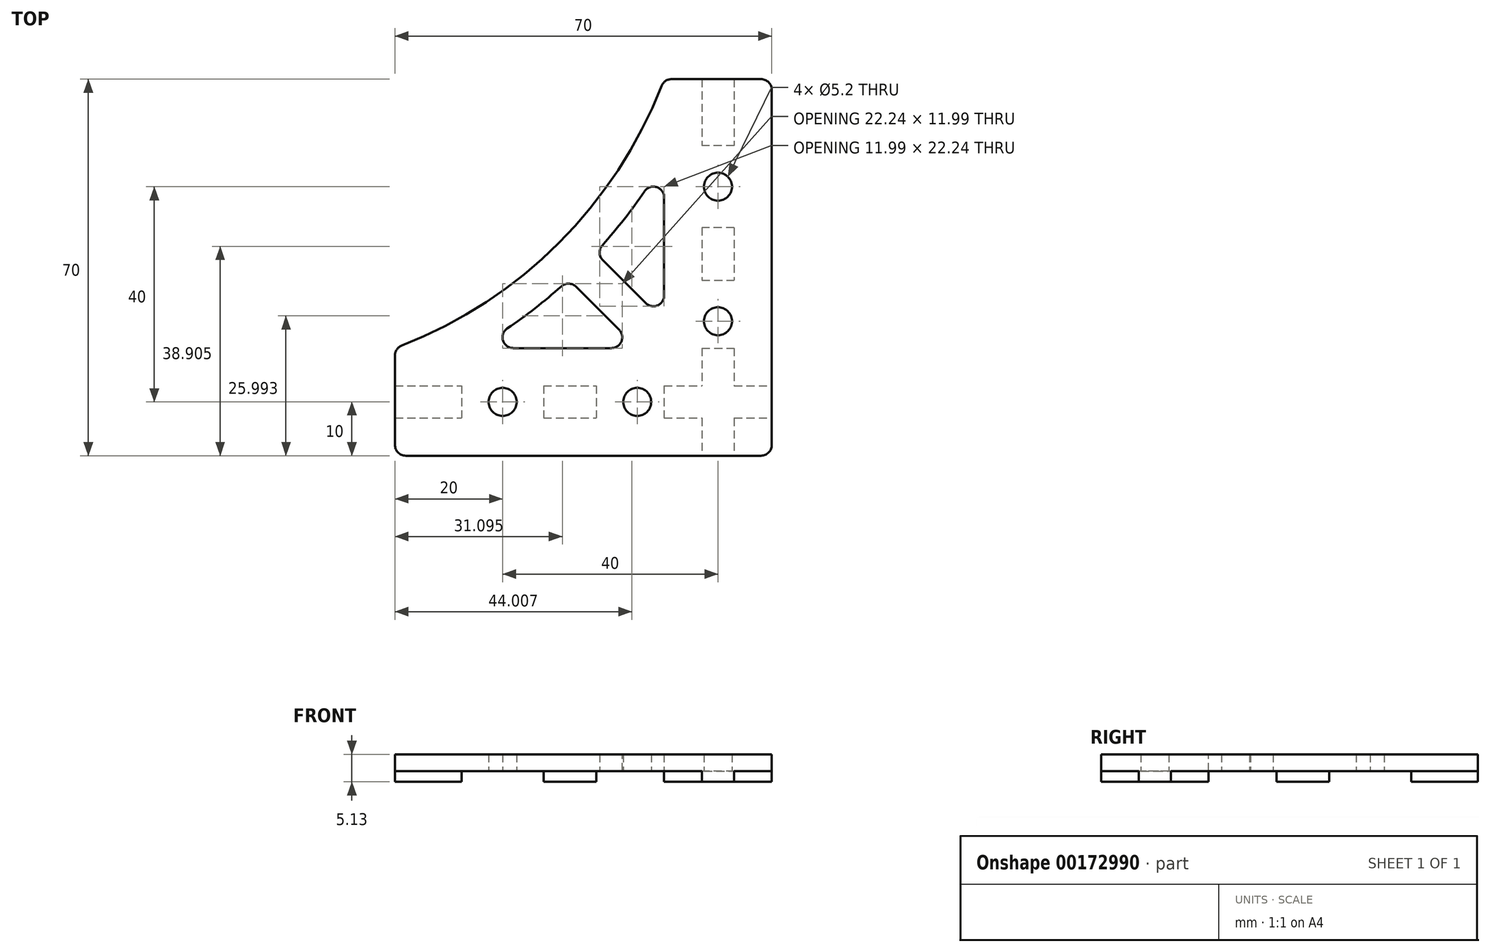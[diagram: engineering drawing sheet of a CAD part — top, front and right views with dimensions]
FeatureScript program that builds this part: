
annotation { "Feature Type Name" : "Feature", "Feature Type Description" : "" }
export const myFeature = defineFeature(function(context is Context, id is Id, definition is map)
    precondition{}
    {
        {
            var Q0;
            Q0=qCreatedBy(makeId("Top.planeOp"),FACE);
            var sketch = newSketch(context, id + "F0", { "sketchPlane" : qUnion([Q0])});
            skLineSegment(sketch, "E0.bottom", {"start": v(-35, 35) * mm, "end": v(35, 35) * mm});
            skLineSegment(sketch, "E0.top", {"start": v(-35, -35) * mm, "end": v(35, -35) * mm});
            skLineSegment(sketch, "E0.left", {"start": v(-35, 35) * mm, "end": v(-35, -35) * mm});
            skLineSegment(sketch, "E0.right", {"start": v(35, 35) * mm, "end": v(35, -35) * mm});
            skPoint(sketch, "E0.middle", {"position": v(0, 0) * mm});
            skLineSegment(sketch, "E1", {"start": v(15, 35) * mm, "end": v(-35, -15) * mm});
            skArc(sketch, "E2", {"start": v(-35, -15) * mm, "mid": v(-4.55, 4.55) * mm, "end": v(15, 35) * mm});
            skSolve(sketch);
        }
        {
            var Q0;
            {var subQ2=sQuery(id+"F0.wireOp",EDGE,"E0.top");Q0=makeQuery(id+"F0.imprint","IMPRINT",FACE,{"disambiguationData":[TD([[makeQuery(id+"F0.imprint","IMPRINT",EDGE,{"derivedFrom":subQ2}),1.0]])]});}
            var Q1;
            {var subQ0=sQuery(id+"F0.wireOp",EDGE,"E0.right");var subQ1=sQuery(id+"F0.wireOp",EDGE,"E0.bottom");var subQ2=makeQuery(id+"F0.imprint","INTERSECT",VERTEX,{"derivedFrom":[subQ1,subQ0]});Q1=makeQuery(id+"F0.imprint","IMPRINT",FACE,{"disambiguationData":[TD([[makeQuery(id+"F0.imprint","IMPRINT",EDGE,{"disambiguationData":[TD([[subQ2,-1.0]])],"derivedFrom":subQ0}),-1.0]])]});}
            var Q2;
            {var subQ1=sQuery(id+"F0.wireOp",EDGE,"E0.right");var subQ5=sQuery(id+"F0.wireOp",EDGE,"E0.top");var subQ6=makeQuery(id+"F0.imprint","INTERSECT",VERTEX,{"derivedFrom":[subQ5,subQ1]});Q2=makeQuery(id+"F0.imprint","IMPRINT",FACE,{"disambiguationData":[TD([[makeQuery(id+"F0.imprint","IMPRINT",EDGE,{"disambiguationData":[TD([[subQ6,1.0]])],"derivedFrom":subQ5}),1.0]])]});}
            extrude(context, id + "F1", {"entities" : qUnion([Q0, Q1, Q2]), "depth" : 3.12 * mm});
        }
        {
            var Q0;
            Q0=makeQuery(id+"F1.opExtrude","CAP_FACE",FACE,{"disambiguationData":[OSD([sQuery(id+"F0.wireOp",EDGE,"E0.bottom"),sQuery(id+"F0.wireOp",EDGE,"E0.top"),sQuery(id+"F0.wireOp",EDGE,"E0.left"),sQuery(id+"F0.wireOp",EDGE,"E0.right"),sQuery(id+"F0.wireOp",EDGE,"E1")])],"isStart":true});
            var sketch = newSketch(context, id + "F2", { "sketchPlane" : qUnion([Q0])});
            skLineSegment(sketch, "E3", {"start": v(25, -35) * mm, "end": v(25, 35) * mm, "construction": true});
            skLineSegment(sketch, "E4", {"start": v(-35, 25) * mm, "end": v(35, 25) * mm, "construction": true});
            skLineSegment(sketch, "E5.bottom", {"start": v(22, -35) * mm, "end": v(28, -35) * mm});
            skLineSegment(sketch, "E5.top", {"start": v(22, 35) * mm, "end": v(28, 35) * mm});
            skLineSegment(sketch, "E5.left", {"start": v(22, -35) * mm, "end": v(22, 35) * mm});
            skLineSegment(sketch, "E5.right", {"start": v(28, -35) * mm, "end": v(28, 35) * mm});
            skPoint(sketch, "E5.middle", {"position": v(25, 0) * mm});
            skLineSegment(sketch, "E6.bottom", {"start": v(-35, 22) * mm, "end": v(35, 22) * mm});
            skLineSegment(sketch, "E6.top", {"start": v(-35, 28) * mm, "end": v(35, 28) * mm});
            skLineSegment(sketch, "E6.left", {"start": v(-35, 22) * mm, "end": v(-35, 28) * mm});
            skLineSegment(sketch, "E6.right", {"start": v(35, 22) * mm, "end": v(35, 28) * mm});
            skPoint(sketch, "E6.middle", {"position": v(0, 25) * mm});
            skLineSegment(sketch, "E7.bottom", {"start": v(22, 22) * mm, "end": v(15, 22) * mm});
            skLineSegment(sketch, "E7.top", {"start": v(22, 28) * mm, "end": v(15, 28) * mm});
            skLineSegment(sketch, "E7.left", {"start": v(22, 22) * mm, "end": v(22, 28) * mm});
            skLineSegment(sketch, "E7.right", {"start": v(15, 22) * mm, "end": v(15, 28) * mm});
            skLineSegment(sketch, "E8.bottom", {"start": v(28, 22) * mm, "end": v(22, 22) * mm});
            skLineSegment(sketch, "E8.top", {"start": v(28, 15) * mm, "end": v(22, 15) * mm});
            skLineSegment(sketch, "E8.left", {"start": v(28, 22) * mm, "end": v(28, 15) * mm});
            skLineSegment(sketch, "E8.right", {"start": v(22, 22) * mm, "end": v(22, 15) * mm});
            skSolve(sketch);
        }
        {
            var Q0;
            {var subQ0=sQuery(id+"F2.wireOp",EDGE,"E5.bottom");Q0=makeQuery(id+"F2.imprint","IMPRINT",FACE,{"disambiguationData":[TD([[makeQuery(id+"F2.imprint","IMPRINT",EDGE,{"derivedFrom":subQ0}),1.0]])]});}
            var Q1;
            {var subQ0=sQuery(id+"F2.wireOp",EDGE,"E6.left");Q1=makeQuery(id+"F2.imprint","IMPRINT",FACE,{"disambiguationData":[TD([[makeQuery(id+"F2.imprint","IMPRINT",EDGE,{"derivedFrom":subQ0}),-1.0]])]});}
            var Q2;
            {var subQ0=sQuery(id+"F2.wireOp",EDGE,"E8.top");Q2=makeQuery(id+"F2.imprint","IMPRINT",FACE,{"disambiguationData":[TD([[makeQuery(id+"F2.imprint","IMPRINT",EDGE,{"derivedFrom":subQ0}),1.0]])]});}
            var Q3;
            {var subQ0=sQuery(id+"F2.wireOp",EDGE,"d9nGMlHh-qkIi-XzYH-rveG-kUuO3HYsBL67");var subQ1=sQuery(id+"F2.wireOp",EDGE,"E5.left");var subQ2=makeQuery(id+"F2.imprint","INTERSECT",VERTEX,{"derivedFrom":[subQ1,subQ0]});Q3=makeQuery(id+"F2.imprint","IMPRINT",FACE,{"disambiguationData":[TD([[makeQuery(id+"F2.imprint","IMPRINT",EDGE,{"disambiguationData":[TD([[subQ2,-1.0]])],"derivedFrom":subQ1}),-1.0]])]});}
            var Q4;
            {var subQ0=sQuery(id+"F2.wireOp",EDGE,"E7.right");Q4=makeQuery(id+"F2.imprint","IMPRINT",FACE,{"disambiguationData":[TD([[makeQuery(id+"F2.imprint","IMPRINT",EDGE,{"derivedFrom":subQ0}),1.0]])]});}
            var Q5;
            {var subQ0=sQuery(id+"F2.wireOp",EDGE,"Tg9qOg1b-ZZ8D-OlWz-hFwT-lKIjL2JHWv4c");var subQ1=sQuery(id+"F2.wireOp",EDGE,"E6.bottom");var subQ2=makeQuery(id+"F2.imprint","INTERSECT",VERTEX,{"derivedFrom":[subQ1,subQ0]});Q5=makeQuery(id+"F2.imprint","IMPRINT",FACE,{"disambiguationData":[TD([[makeQuery(id+"F2.imprint","IMPRINT",EDGE,{"disambiguationData":[TD([[subQ2,-1.0]])],"derivedFrom":subQ1}),1.0]])]});}
            extrude(context, id + "F3", {"entities" : qUnion([Q0, Q1, Q2, Q3, Q4, Q5]), "operationType" : NewBodyOperationType.ADD, "depth" : 2 * mm, "offsetDistance" : 25 * mm});
        }
        {
            var Q0;
            Q0=makeQuery(id+"F3.opExtrude","CAP_FACE",FACE,{"disambiguationData":[OSD([sQuery(id+"F2.wireOp",EDGE,"E5.bottom"),sQuery(id+"F2.wireOp",EDGE,"E5.left"),sQuery(id+"F2.wireOp",EDGE,"E5.right"),sQuery(id+"F2.wireOp",EDGE,"E8.top")])],"isStart":false});
            var sketch = newSketch(context, id + "F4", { "sketchPlane" : qUnion([Q0])});
            skCircle(sketch, "E9", {"center": v(25, -15) * mm, "radius": 2.6 * mm});
            skCircle(sketch, "E10", {"center": v(25, 10) * mm, "radius": 2.6 * mm});
            skCircle(sketch, "E11", {"center": v(10, 25) * mm, "radius": 2.6 * mm});
            skCircle(sketch, "E12", {"center": v(-15, 25) * mm, "radius": 2.6 * mm});
            skSolve(sketch);
        }
        {
            var Q0;
            Q0=makeQuery(id+"F4.imprint","IMPRINT",FACE,{"disambiguationData":[TD([[makeQuery(id+"F4.imprint","IMPRINT",EDGE,{"derivedFrom":sQuery(id+"F4.wireOp",EDGE,"E9")}),1.0]])]});
            var Q1;
            Q1=makeQuery(id+"F4.imprint","IMPRINT",FACE,{"disambiguationData":[TD([[makeQuery(id+"F4.imprint","IMPRINT",EDGE,{"derivedFrom":sQuery(id+"F4.wireOp",EDGE,"E10")}),1.0]])]});
            var Q2;
            Q2=makeQuery(id+"F4.imprint","IMPRINT",FACE,{"disambiguationData":[TD([[makeQuery(id+"F4.imprint","IMPRINT",EDGE,{"derivedFrom":sQuery(id+"F4.wireOp",EDGE,"E11")}),1.0]])]});
            var Q3;
            Q3=makeQuery(id+"F4.imprint","IMPRINT",FACE,{"disambiguationData":[TD([[makeQuery(id+"F4.imprint","IMPRINT",EDGE,{"derivedFrom":sQuery(id+"F4.wireOp",EDGE,"E12")}),1.0]])]});
            var Q4;
            Q4=makeQuery(id+"F4.imprint","IMPRINT",FACE,{"disambiguationData":[TD([[makeQuery(id+"F4.imprint","IMPRINT",EDGE,{"derivedFrom":sQuery(id+"F4.wireOp",EDGE,"NlfKYLu6-I90x-wP9U-KteL-I13C1IhuDyRd")}),1.0]])]});
            extrude(context, id + "F5", {"entities" : qUnion([Q0, Q1, Q2, Q3, Q4]), "operationType" : NewBodyOperationType.REMOVE, "oppositeDirection" : true, "depth" : 25 * mm, "offsetDistance" : 25 * mm});
        }
        {
            var Q0;
            Q0=makeQuery(id+"F3.opExtrude","CAP_FACE",FACE,{"disambiguationData":[OSD([sQuery(id+"F2.wireOp",EDGE,"E5.bottom"),sQuery(id+"F2.wireOp",EDGE,"E5.left"),sQuery(id+"F2.wireOp",EDGE,"E5.right"),sQuery(id+"F2.wireOp",EDGE,"E8.top")])],"isStart":false});
            var sketch = newSketch(context, id + "F6", { "sketchPlane" : qUnion([Q0])});
            skLineSegment(sketch, "E13.bottom", {"start": v(22, 15) * mm, "end": v(28, 15) * mm});
            skLineSegment(sketch, "E13.top", {"start": v(22, 2.4) * mm, "end": v(28, 2.4) * mm});
            skLineSegment(sketch, "E13.left", {"start": v(22, 15) * mm, "end": v(22, 2.4) * mm});
            skLineSegment(sketch, "E13.right", {"start": v(28, 15) * mm, "end": v(28, 2.4) * mm});
            skLineSegment(sketch, "E14.bottom", {"start": v(28, -7.4) * mm, "end": v(22, -7.4) * mm});
            skLineSegment(sketch, "E14.top", {"start": v(28, -22.6) * mm, "end": v(22, -22.6) * mm});
            skLineSegment(sketch, "E14.left", {"start": v(28, -7.4) * mm, "end": v(28, -22.6) * mm});
            skLineSegment(sketch, "E14.right", {"start": v(22, -7.4) * mm, "end": v(22, -22.6) * mm});
            skSolve(sketch);
        }
        {
            var Q0;
            Q0 = qSketchRegion(id + "F6", true);
            extrude(context, id + "F7", {"entities" : qUnion([Q0]), "operationType" : NewBodyOperationType.REMOVE, "oppositeDirection" : true, "depth" : 2 * mm, "offsetDistance" : 25 * mm});
        }
        {
            var Q0;
            Q0=makeQuery(id+"F3.opExtrude","CAP_FACE",FACE,{"disambiguationData":[OSD([sQuery(id+"F2.wireOp",EDGE,"E6.bottom"),sQuery(id+"F2.wireOp",EDGE,"E6.top"),sQuery(id+"F2.wireOp",EDGE,"E6.left"),sQuery(id+"F2.wireOp",EDGE,"E7.right")])],"isStart":false});
            var sketch = newSketch(context, id + "F8", { "sketchPlane" : qUnion([Q0])});
            skLineSegment(sketch, "E15.bottom", {"start": v(15, 22) * mm, "end": v(2.4, 22) * mm});
            skLineSegment(sketch, "E15.top", {"start": v(15, 28) * mm, "end": v(2.4, 28) * mm});
            skLineSegment(sketch, "E15.left", {"start": v(15, 22) * mm, "end": v(15, 28) * mm});
            skLineSegment(sketch, "E15.right", {"start": v(2.4, 22) * mm, "end": v(2.4, 28) * mm});
            skLineSegment(sketch, "E16.bottom", {"start": v(-7.4, 22) * mm, "end": v(-22.6, 22) * mm});
            skLineSegment(sketch, "E16.top", {"start": v(-7.4, 28) * mm, "end": v(-22.6, 28) * mm});
            skLineSegment(sketch, "E16.left", {"start": v(-7.4, 22) * mm, "end": v(-7.4, 28) * mm});
            skLineSegment(sketch, "E16.right", {"start": v(-22.6, 22) * mm, "end": v(-22.6, 28) * mm});
            skSolve(sketch);
        }
        {
            var Q0;
            Q0 = qSketchRegion(id + "F8", true);
            extrude(context, id + "F9", {"entities" : qUnion([Q0]), "operationType" : NewBodyOperationType.REMOVE, "oppositeDirection" : true, "depth" : 2 * mm, "offsetDistance" : 25 * mm});
        }
        {
            var Q0;
            Q0=makeQuery(id+"F1.opExtrude","SWEPT_EDGE",EDGE,{"disambiguationData":[OSD([sQuery(id+"F0.wireOp",EDGE,"E0.bottom"),sQuery(id+"F0.wireOp",EDGE,"E0.right")])]});
            var Q1;
            Q1=makeQuery(id+"F1.opExtrude","SWEPT_EDGE",EDGE,{"disambiguationData":[OSD([sQuery(id+"F0.wireOp",EDGE,"E0.bottom"),sQuery(id+"F0.wireOp",EDGE,"E1")])]});
            var Q2;
            Q2=makeQuery(id+"F1.opExtrude","SWEPT_EDGE",EDGE,{"disambiguationData":[OSD([sQuery(id+"F0.wireOp",EDGE,"E0.left"),sQuery(id+"F0.wireOp",EDGE,"E1")])]});
            var Q3;
            Q3=makeQuery(id+"F1.opExtrude","SWEPT_EDGE",EDGE,{"disambiguationData":[OSD([sQuery(id+"F0.wireOp",EDGE,"E0.top"),sQuery(id+"F0.wireOp",EDGE,"E0.left")])]});
            var Q4;
            Q4=makeQuery(id+"F1.opExtrude","SWEPT_EDGE",EDGE,{"disambiguationData":[OSD([sQuery(id+"F0.wireOp",EDGE,"E0.top"),sQuery(id+"F0.wireOp",EDGE,"E0.right")])]});
            fillet(context, id + "F10", {"entities" : qUnion([Q0, Q1, Q2, Q3, Q4]), "radius" : 2 * mm, "tangentPropagation" : true, "allowEdgeOverflow" : false});
        }
        {
            var Q0;
            Q0=qCreatedBy(makeId("Top.planeOp"),FACE);
            var sketch = newSketch(context, id + "F11", { "sketchPlane" : qUnion([Q0])});
            skLineSegment(sketch, "E17.bottom", {"start": v(15, 20) * mm, "end": v(-20, 20) * mm});
            skLineSegment(sketch, "E17.top", {"start": v(15, -15) * mm, "end": v(-20, -15) * mm});
            skLineSegment(sketch, "E17.left", {"start": v(15, 20) * mm, "end": v(15, -15) * mm});
            skLineSegment(sketch, "E17.right", {"start": v(-20, 20) * mm, "end": v(-20, -15) * mm});
            skLineSegment(sketch, "E18", {"start": v(15, 20) * mm, "end": v(-20, -15) * mm});
            skArc(sketch, "E19", {"start": v(-20, -15) * mm, "mid": v(-0.18, 0.18) * mm, "end": v(15, 20) * mm});
            skLineSegment(sketch, "E20", {"start": v(0, 0) * mm, "end": v(36.97, -36.97) * mm, "construction": true});
            skLineSegment(sketch, "E21", {"start": v(-0.03, 4.97) * mm, "end": v(42.01, -37.06) * mm});
            skLineSegment(sketch, "E22", {"start": v(-4.97, 0.03) * mm, "end": v(36.42, -41.37) * mm});
            skSolve(sketch);
        }
        {
            var Q0;
            Q0=makeQuery(id+"F11.imprint","IMPRINT",FACE,{"disambiguationData":[TD([[makeQuery(id+"F11.imprint","IMPRINT",EDGE,{"derivedFrom":sQuery(id+"F11.wireOp",EDGE,"E17.top")}),-1.0]])]});
            var Q1;
            {var subQ1=sQuery(id+"F11.wireOp",EDGE,"E17.left");var subQ3=sQuery(id+"F11.wireOp",EDGE,"E21");var subQ4=makeQuery(id+"F11.imprint","INTERSECT",VERTEX,{"derivedFrom":[subQ1,subQ3]});Q1=makeQuery(id+"F11.imprint","IMPRINT",FACE,{"disambiguationData":[TD([[makeQuery(id+"F11.imprint","IMPRINT",EDGE,{"disambiguationData":[TD([[subQ4,1.0]])],"derivedFrom":subQ3}),1.0]])]});}
            extrude(context, id + "F12", {"entities" : qUnion([Q0, Q1]), "operationType" : NewBodyOperationType.REMOVE, "depth" : 25 * mm});
        }
        {
            var Q0;
            Q0=makeQuery(id+"F12.boolean.opBoolean","COPY",EDGE,{"derivedFrom":makeQuery(id+"F12.opExtrude","SWEPT_EDGE",EDGE,{"disambiguationData":[OSD([sQuery(id+"F11.wireOp",EDGE,"E17.bottom"),sQuery(id+"F11.wireOp",EDGE,"E17.left"),sQuery(id+"F11.wireOp",EDGE,"E18")])]})});
            var Q1;
            Q1=makeQuery(id+"F12.boolean.opBoolean","COPY",EDGE,{"derivedFrom":makeQuery(id+"F12.opExtrude","SWEPT_EDGE",EDGE,{"disambiguationData":[OSD([sQuery(id+"F11.wireOp",EDGE,"E17.top"),sQuery(id+"F11.wireOp",EDGE,"E17.left")])]})});
            var Q2;
            Q2=makeQuery(id+"F12.boolean.opBoolean","COPY",EDGE,{"derivedFrom":makeQuery(id+"F12.opExtrude","SWEPT_EDGE",EDGE,{"disambiguationData":[OSD([sQuery(id+"F11.wireOp",EDGE,"E17.top"),sQuery(id+"F11.wireOp",EDGE,"E17.right"),sQuery(id+"F11.wireOp",EDGE,"E18")])]})});
            var Q3;
            Q3=makeQuery(id+"F12.boolean.opBoolean","COPY",EDGE,{"derivedFrom":makeQuery(id+"F12.opExtrude","SWEPT_EDGE",EDGE,{"disambiguationData":[OSD([sQuery(id+"F11.wireOp",EDGE,"E19"),sQuery(id+"F11.wireOp",EDGE,"E21")])]})});
            var Q4;
            Q4=makeQuery(id+"F12.boolean.opBoolean","COPY",EDGE,{"derivedFrom":makeQuery(id+"F12.opExtrude","SWEPT_EDGE",EDGE,{"disambiguationData":[OSD([sQuery(id+"F11.wireOp",EDGE,"E19"),sQuery(id+"F11.wireOp",EDGE,"E22")])]})});
            fillet(context, id + "F13", {"entities" : qUnion([Q0, Q1, Q2, Q3, Q4]), "radius" : 2 * mm, "tangentPropagation" : true, "allowEdgeOverflow" : false});
        }
    });
